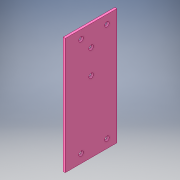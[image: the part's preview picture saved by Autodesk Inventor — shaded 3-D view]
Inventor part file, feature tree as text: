
AUTODESK INVENTOR PART (.ipt)
format: ipt  version: 2016 (Build 200138000, 138)  size: 117,760 bytes
history: native  units: in
note: dims shown in document units (in); Inventor stores cm internally (conversion verified against a paired STEP export)
features: extrude x2, sketch x2
ambient origin geometry x8: Origin, YZ Plane, XZ Plane, XY Plane, X Axis, Y Axis, Z Axis, Center Point
bodies: Solid1 (feature_tree)
feature tree (4):
  extrude  "Extrusion1"  Depth=3.0in
  extrude  "Extrusion2"  Depth=0.125in
  sketch  "Sketch1"  dims[d0=6.75in d1=3.0in]
  sketch  "Sketch2"  dims[d2=0.125in d3=0.0in d4=0.2656in d5=1.211in d6=1.5in d7=0.2656in d8=1.5in d9=1.4142in d10=0.125in d11=0.0in d12=0.2656in d13=0.582in d14=0.5in d15=0.2656in d16=1.5in d17=0.5in d18=0.582in d19=1.5in d20=0.5in d21=0.5in]
